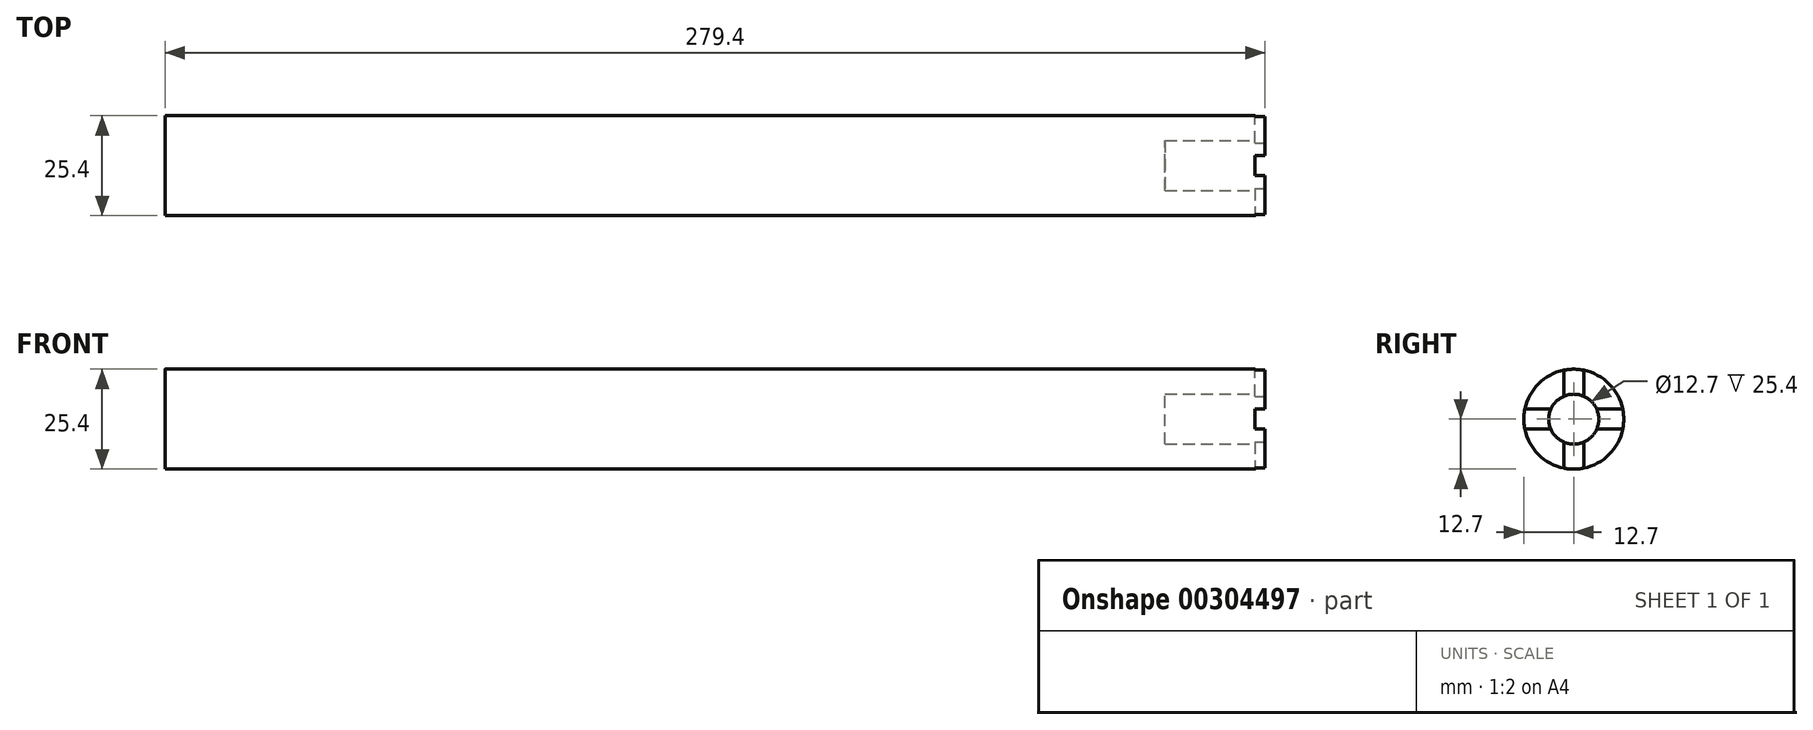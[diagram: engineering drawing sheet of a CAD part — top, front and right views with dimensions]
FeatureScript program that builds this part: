
annotation { "Feature Type Name" : "Feature", "Feature Type Description" : "" }
export const myFeature = defineFeature(function(context is Context, id is Id, definition is map)
    precondition{}
    {
        {
            var Q0;
            Q0=qCreatedBy(makeId("Right.planeOp"),FACE);
            var sketch = newSketch(context, id + "F0", { "sketchPlane" : qUnion([Q0])});
            skCircle(sketch, "E0", {"center": v(0, 0) * mm, "radius": 12.7 * mm});
            skSolve(sketch);
        }
        {
            var Q0;
            Q0 = qSketchRegion(id + "F0", true);
            extrude(context, id + "F1", {"entities" : qUnion([Q0]), "depth" : 279.4 * mm});
        }
        {
            var Q0;
            Q0=makeQuery(id+"F1.opExtrude","CAP_FACE",FACE,{"disambiguationData":[OSD([sQuery(id+"F0.wireOp",EDGE,"E0")])],"isStart":false});
            var sketch = newSketch(context, id + "F2", { "sketchPlane" : qUnion([Q0])});
            skCircle(sketch, "E1", {"center": v(0, 0) * mm, "radius": 6.35 * mm});
            skSolve(sketch);
        }
        {
            var Q0;
            Q0 = qSketchRegion(id + "F2", true);
            extrude(context, id + "F3", {"entities" : qUnion([Q0]), "operationType" : NewBodyOperationType.REMOVE, "oppositeDirection" : true, "depth" : 25.4 * mm});
        }
        {
            var Q0;
            Q0=makeQuery(id+"F1.opExtrude","CAP_FACE",FACE,{"disambiguationData":[OSD([sQuery(id+"F0.wireOp",EDGE,"E0")])],"isStart":false});
            var sketch = newSketch(context, id + "F4", { "sketchPlane" : qUnion([Q0])});
            skLineSegment(sketch, "E2.top", {"start": v(-2.54, 14.94) * mm, "end": v(2.54, 14.94) * mm});
            skLineSegment(sketch, "E2.left", {"start": v(-2.54, 2.54) * mm, "end": v(-2.54, 14.94) * mm});
            skLineSegment(sketch, "E2.right", {"start": v(2.54, 2.54) * mm, "end": v(2.54, 14.94) * mm});
            skPoint(sketch, "E3.firstSnap0", {"position": v(0, 0) * mm});
            skLineSegment(sketch, "E3.bottom", {"start": v(-2.54, 2.54) * mm, "end": v(-16.36, 2.54) * mm});
            skLineSegment(sketch, "E3.top", {"start": v(-2.54, -2.54) * mm, "end": v(-16.36, -2.54) * mm});
            skLineSegment(sketch, "E3.right", {"start": v(-16.36, 2.54) * mm, "end": v(-16.36, -2.54) * mm});
            skLineSegment(sketch, "E4.top", {"start": v(-2.54, -16.47) * mm, "end": v(2.54, -16.47) * mm});
            skLineSegment(sketch, "E4.left", {"start": v(-2.54, -2.54) * mm, "end": v(-2.54, -16.47) * mm});
            skLineSegment(sketch, "E4.right", {"start": v(2.54, -2.54) * mm, "end": v(2.54, -16.47) * mm});
            skLineSegment(sketch, "E5.bottom", {"start": v(2.54, 2.54) * mm, "end": v(18.68, 2.54) * mm});
            skLineSegment(sketch, "E5.top", {"start": v(2.54, -2.54) * mm, "end": v(18.68, -2.54) * mm});
            skLineSegment(sketch, "E5.right", {"start": v(18.68, 2.54) * mm, "end": v(18.68, -2.54) * mm});
            skLineSegment(sketch, "E6", {"start": v(-2.54, 2.54) * mm, "end": v(2.54, 2.54) * mm, "construction": true});
            skLineSegment(sketch, "E7", {"start": v(0, 2.54) * mm, "end": v(0, -2.54) * mm, "construction": true});
            skLineSegment(sketch, "E8", {"start": v(0, -2.54) * mm, "end": v(-2.54, -2.54) * mm, "construction": true});
            skLineSegment(sketch, "E9", {"start": v(2.54, -2.54) * mm, "end": v(-2.54, -2.54) * mm, "construction": true});
            skLineSegment(sketch, "E10", {"start": v(-2.54, 2.54) * mm, "end": v(-2.54, -2.54) * mm, "construction": true});
            skLineSegment(sketch, "E11", {"start": v(2.54, 2.54) * mm, "end": v(2.54, -2.54) * mm, "construction": true});
            skLineSegment(sketch, "E12", {"start": v(-2.54, 0) * mm, "end": v(2.54, 0) * mm, "construction": true});
            skSolve(sketch);
        }
        {
            var Q0;
            Q0 = qSketchRegion(id + "F4", true);
            extrude(context, id + "F5", {"entities" : qUnion([Q0]), "operationType" : NewBodyOperationType.REMOVE, "oppositeDirection" : true, "depth" : 2.54 * mm});
        }
    });
